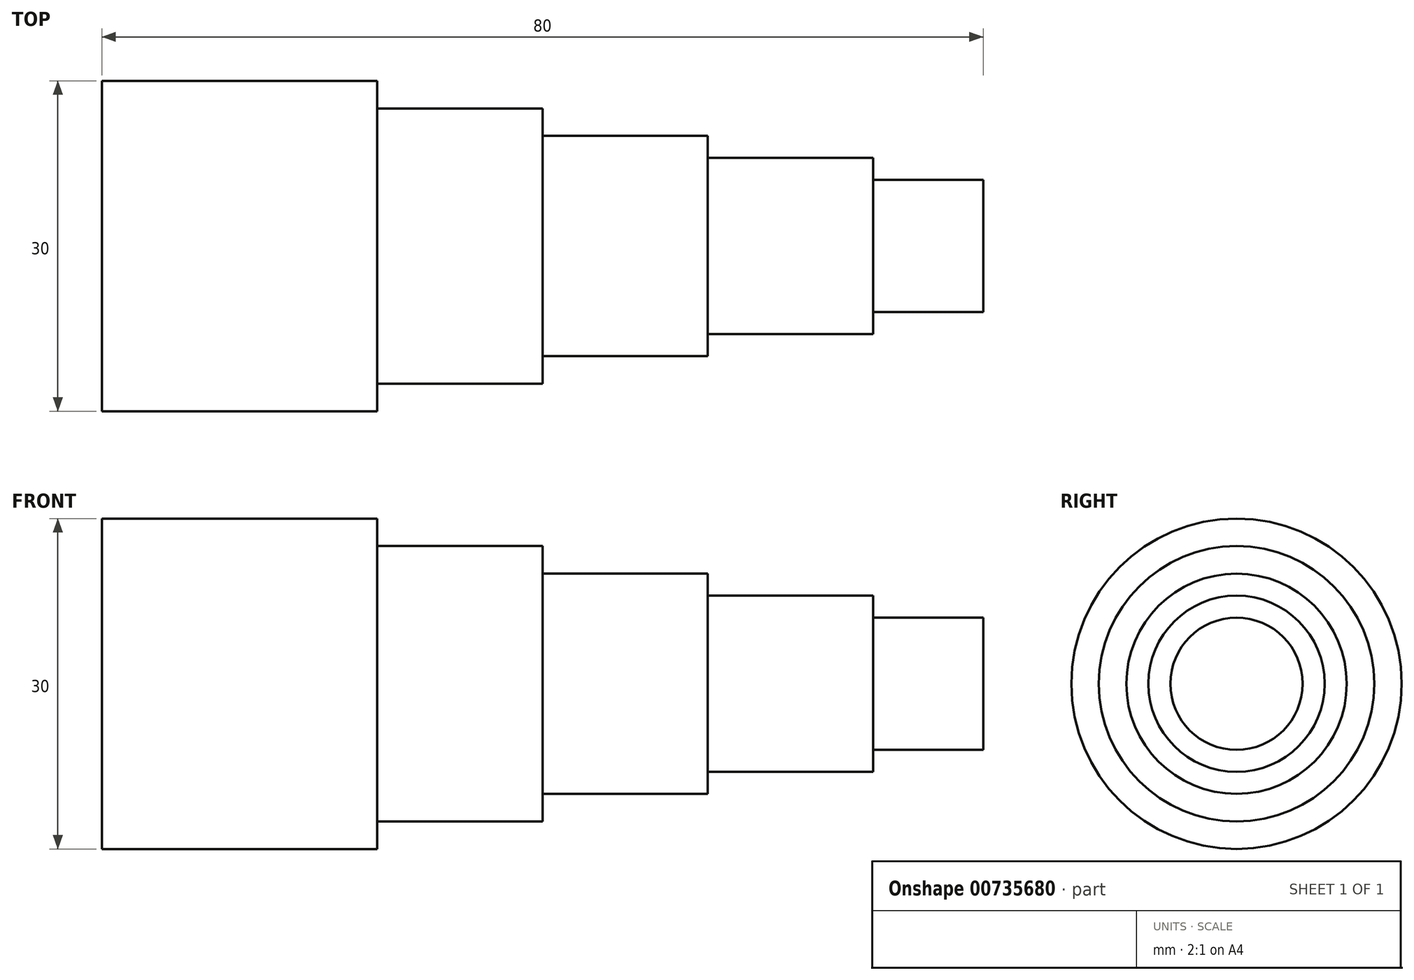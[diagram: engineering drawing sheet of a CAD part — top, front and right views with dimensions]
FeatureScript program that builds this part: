
annotation { "Feature Type Name" : "Feature", "Feature Type Description" : "" }
export const myFeature = defineFeature(function(context is Context, id is Id, definition is map)
    precondition{}
    {
        {
            var Q0;
            Q0=qCreatedBy(makeId("Top.planeOp"),FACE);
            var sketch = newSketch(context, id + "F0", { "sketchPlane" : qUnion([Q0])});
            skLineSegment(sketch, "E0.bottom", {"start": v(27.54, 8.51) * mm, "end": v(37.54, 8.51) * mm});
            skLineSegment(sketch, "E0.top", {"start": v(27.54, 2.51) * mm, "end": v(37.54, 2.51) * mm});
            skLineSegment(sketch, "E0.left", {"start": v(27.54, 8.51) * mm, "end": v(27.54, 2.51) * mm});
            skLineSegment(sketch, "E0.right", {"start": v(37.54, 8.51) * mm, "end": v(37.54, 2.51) * mm});
            skLineSegment(sketch, "E1.bottom", {"start": v(12.54, 10.51) * mm, "end": v(27.54, 10.51) * mm});
            skLineSegment(sketch, "E1.top", {"start": v(12.54, 2.51) * mm, "end": v(27.54, 2.51) * mm});
            skLineSegment(sketch, "E1.left", {"start": v(12.54, 10.51) * mm, "end": v(12.54, 2.51) * mm});
            skLineSegment(sketch, "E1.right", {"start": v(27.54, 10.51) * mm, "end": v(27.54, 2.51) * mm});
            skLineSegment(sketch, "E2.bottom", {"start": v(-2.46, 12.51) * mm, "end": v(12.54, 12.51) * mm});
            skLineSegment(sketch, "E2.top", {"start": v(-2.46, 2.51) * mm, "end": v(12.54, 2.51) * mm});
            skLineSegment(sketch, "E2.left", {"start": v(-2.46, 12.51) * mm, "end": v(-2.46, 2.51) * mm});
            skLineSegment(sketch, "E2.right", {"start": v(12.54, 12.51) * mm, "end": v(12.54, 2.51) * mm});
            skLineSegment(sketch, "E3.bottom", {"start": v(-17.46, 15.01) * mm, "end": v(-2.46, 15.01) * mm});
            skLineSegment(sketch, "E3.top", {"start": v(-17.46, 2.51) * mm, "end": v(-2.46, 2.51) * mm});
            skLineSegment(sketch, "E3.left", {"start": v(-17.46, 15.01) * mm, "end": v(-17.46, 2.51) * mm});
            skLineSegment(sketch, "E3.right", {"start": v(-2.46, 15.01) * mm, "end": v(-2.46, 2.51) * mm});
            skLineSegment(sketch, "E4.bottom", {"start": v(-42.46, 17.51) * mm, "end": v(-17.46, 17.51) * mm});
            skLineSegment(sketch, "E4.top", {"start": v(-42.46, 2.51) * mm, "end": v(-17.46, 2.51) * mm});
            skLineSegment(sketch, "E4.left", {"start": v(-42.46, 17.51) * mm, "end": v(-42.46, 2.51) * mm});
            skLineSegment(sketch, "E4.right", {"start": v(-17.46, 17.51) * mm, "end": v(-17.46, 2.51) * mm});
            skLineSegment(sketch, "E5.right", {"start": v(-42.46, 16) * mm, "end": v(-42.46, 2.51) * mm});
            skSolve(sketch);
        }
        {
            var Q0;
            Q0 = qSketchRegion(id + "F0", true);
            var Q1;
            Q1=sQuery(id+"F0.wireOp",EDGE,"E1.top");
            revolve(context, id + "F1", {"surfaceOperationType" : NewSurfaceOperationType.NEW, "entities" : qUnion([Q0]), "axis" : qUnion([Q1]), "revolveType" : RevolveType.FULL});
        }
    });
